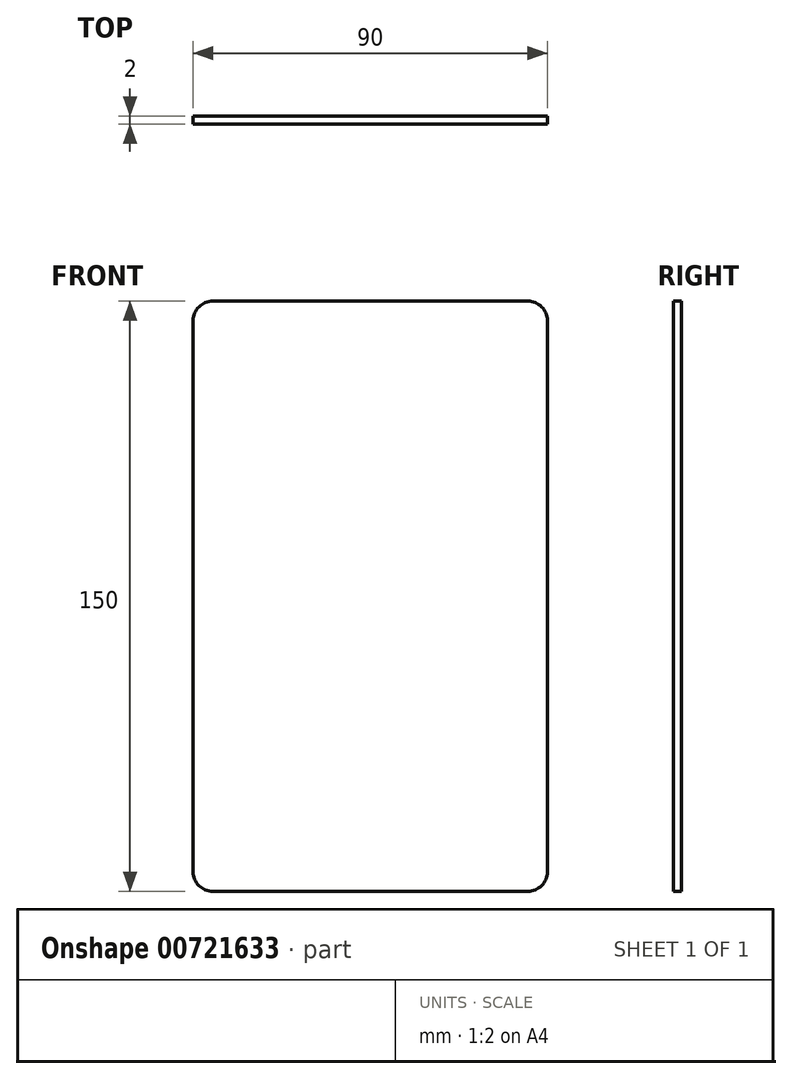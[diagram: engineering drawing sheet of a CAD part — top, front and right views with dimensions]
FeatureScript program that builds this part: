
annotation { "Feature Type Name" : "Feature", "Feature Type Description" : "" }
export const myFeature = defineFeature(function(context is Context, id is Id, definition is map)
    precondition{}
    {
        {
            var Q0;
            Q0=qCreatedBy(makeId("Front.planeOp"),FACE);
            var sketch = newSketch(context, id + "F0", { "sketchPlane" : qUnion([Q0])});
            skLineSegment(sketch, "E0.bottom", {"start": v(5, 0) * mm, "end": v(85, 0) * mm});
            skLineSegment(sketch, "E0.top", {"start": v(5, 150) * mm, "end": v(85, 150) * mm});
            skLineSegment(sketch, "E0.left", {"start": v(0, 5) * mm, "end": v(0, 145) * mm});
            skLineSegment(sketch, "E0.right", {"start": v(90, 5) * mm, "end": v(90, 145) * mm});
            skPoint(sketch, "E1.visualSharp", {"position": v(0, 150) * mm});
            skArc(sketch, "E1.filletArc", {"start": v(5, 150) * mm, "mid": v(1.46, 148.54) * mm, "end": v(0, 145) * mm});
            skPoint(sketch, "E2.visualSharp", {"position": v(90, 150) * mm});
            skArc(sketch, "E2.filletArc", {"start": v(90, 145) * mm, "mid": v(88.54, 148.54) * mm, "end": v(85, 150) * mm});
            skPoint(sketch, "E3.visualSharp", {"position": v(90, 0) * mm});
            skArc(sketch, "E3.filletArc", {"start": v(85, 0) * mm, "mid": v(88.54, 1.46) * mm, "end": v(90, 5) * mm});
            skPoint(sketch, "E4.visualSharp", {"position": v(0, 0) * mm});
            skArc(sketch, "E4.filletArc", {"start": v(0, 5) * mm, "mid": v(1.46, 1.46) * mm, "end": v(5, 0) * mm});
            skSolve(sketch);
        }
        {
            var Q0;
            Q0=makeQuery(id+"F0.imprint","IMPRINT",FACE,{"disambiguationData":[TD([[makeQuery(id+"F0.imprint","IMPRINT",EDGE,{"derivedFrom":sQuery(id+"F0.wireOp",EDGE,"E0.bottom")}),1.0]])]});
            extrude(context, id + "F1", {"entities" : qUnion([Q0]), "depth" : 2 * mm, "offsetDistance" : 25 * mm});
        }
    });
